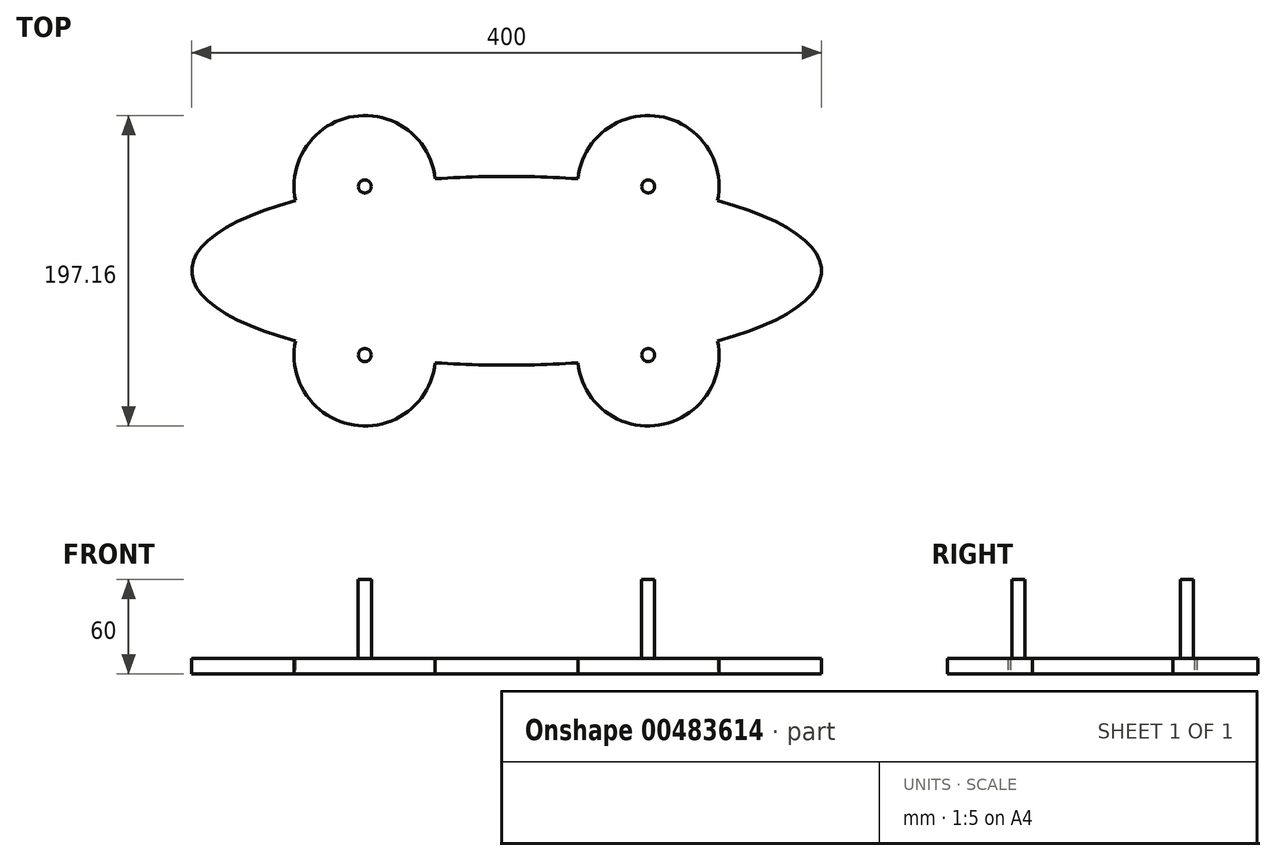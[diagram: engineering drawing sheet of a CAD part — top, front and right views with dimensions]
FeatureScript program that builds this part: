
annotation { "Feature Type Name" : "Feature", "Feature Type Description" : "" }
export const myFeature = defineFeature(function(context is Context, id is Id, definition is map)
    precondition{}
    {
        {
            var Q0;
            Q0=qCreatedBy(makeId("Top.planeOp"),FACE);
            var sketch = newSketch(context, id + "F0", { "sketchPlane" : qUnion([Q0])});
            skLineSegment(sketch, "E0.bottom", {"start": v(200, 100) * mm, "end": v(-200, 100) * mm});
            skLineSegment(sketch, "E0.top", {"start": v(200, -100) * mm, "end": v(-200, -100) * mm});
            skLineSegment(sketch, "E0.left", {"start": v(200, 100) * mm, "end": v(200, -100) * mm});
            skLineSegment(sketch, "E0.right", {"start": v(-200, 100) * mm, "end": v(-200, -100) * mm});
            skPoint(sketch, "E0.middle", {"position": v(0, 0) * mm});
            skLineSegment(sketch, "E1.bottom", {"start": v(200, 60) * mm, "end": v(-200, 60) * mm});
            skLineSegment(sketch, "E1.top", {"start": v(200, -60) * mm, "end": v(-200, -60) * mm});
            skLineSegment(sketch, "E1.left", {"start": v(200, 60) * mm, "end": v(200, -60) * mm});
            skLineSegment(sketch, "E1.right", {"start": v(-200, 60) * mm, "end": v(-200, -60) * mm});
            skPoint(sketch, "E2", {"position": v(200, 0) * mm});
            skPoint(sketch, "E3", {"position": v(0, 60) * mm});
            skEllipse(sketch, "E4", {"center": v(0, 0) * mm, "majorRadius": 200 * mm, "minorRadius": 60 * mm, "majorAxis": v(1, 0)});
            skLineSegment(sketch, "E5.bottom", {"start": v(90, 53.58) * mm, "end": v(-90, 53.58) * mm});
            skLineSegment(sketch, "E5.top", {"start": v(90, -53.58) * mm, "end": v(-90, -53.58) * mm});
            skLineSegment(sketch, "E5.left", {"start": v(90, 53.58) * mm, "end": v(90, -53.58) * mm});
            skLineSegment(sketch, "E5.right", {"start": v(-90, 53.58) * mm, "end": v(-90, -53.58) * mm});
            skCircle(sketch, "E6", {"center": v(-90, 53.58) * mm, "radius": 45 * mm});
            skCircle(sketch, "E7.1.0.0", {"center": v(90, 53.58) * mm, "radius": 45 * mm});
            skLineSegment(sketch, "E7.direction1", {"start": v(-90, 53.58) * mm, "end": v(90, 53.58) * mm, "construction": true});
            skCircle(sketch, "E8.0.1.0", {"center": v(90, -53.58) * mm, "radius": 45 * mm});
            skCircle(sketch, "E8.0.1.1", {"center": v(-90, -53.58) * mm, "radius": 45 * mm});
            skLineSegment(sketch, "E8.direction1", {"start": v(-90, 53.58) * mm, "end": v(-65, 53.58) * mm, "construction": true});
            skLineSegment(sketch, "E8.direction2", {"start": v(-90, 53.58) * mm, "end": v(-90, -53.58) * mm, "construction": true});
            skSolve(sketch);
        }
        {
            var Q0;
            {var subQ5=sQuery(id+"F0.wireOp",EDGE,"E4");var subQ6=makeQuery(id+"F0.imprint","INTERSECT",VERTEX,{"derivedFrom":[sQuery(id+"F0.wireOp",EDGE,"E1.right"),subQ5]});Q0=makeQuery(id+"F0.imprint","IMPRINT",FACE,{"disambiguationData":[TD([[makeQuery(id+"F0.imprint","IMPRINT",EDGE,{"disambiguationData":[TD([[subQ6,1.0]])],"derivedFrom":subQ5}),1.0]])]});}
            var Q1;
            {var subQ1=sQuery(id+"F0.wireOp",EDGE,"E4");var subQ7=makeQuery(id+"F0.imprint","INTERSECT",VERTEX,{"derivedFrom":[sQuery(id+"F0.wireOp",EDGE,"E1.left"),subQ1]});Q1=makeQuery(id+"F0.imprint","IMPRINT",FACE,{"disambiguationData":[TD([[makeQuery(id+"F0.imprint","IMPRINT",EDGE,{"disambiguationData":[TD([[subQ7,-1.0]])],"derivedFrom":subQ1}),1.0]])]});}
            var Q2;
            {var subQ5=sQuery(id+"F0.wireOp",EDGE,"E7.1.0.0");var subQ6=sQuery(id+"F0.wireOp",EDGE,"E5.bottom");var subQ7=makeQuery(id+"F0.imprint","INTERSECT",VERTEX,{"derivedFrom":[subQ6,subQ5]});Q2=makeQuery(id+"F0.imprint","IMPRINT",FACE,{"disambiguationData":[TD([[makeQuery(id+"F0.imprint","IMPRINT",EDGE,{"disambiguationData":[TD([[subQ7,-1.0]])],"derivedFrom":subQ6}),1.0]])]});}
            var Q3;
            {var subQ1=sQuery(id+"F0.wireOp",EDGE,"E5.bottom");var subQ3=sQuery(id+"F0.wireOp",EDGE,"E7.1.0.0");var subQ4=makeQuery(id+"F0.imprint","INTERSECT",VERTEX,{"derivedFrom":[subQ1,subQ3]});Q3=makeQuery(id+"F0.imprint","IMPRINT",FACE,{"disambiguationData":[TD([[makeQuery(id+"F0.imprint","IMPRINT",EDGE,{"disambiguationData":[TD([[subQ4,-1.0]])],"derivedFrom":subQ3}),1.0]])]});}
            var Q4;
            {var subQ1=sQuery(id+"F0.wireOp",EDGE,"E5.top");var subQ3=sQuery(id+"F0.wireOp",EDGE,"E8.0.1.0");var subQ4=makeQuery(id+"F0.imprint","INTERSECT",VERTEX,{"derivedFrom":[subQ1,subQ3]});Q4=makeQuery(id+"F0.imprint","IMPRINT",FACE,{"disambiguationData":[TD([[makeQuery(id+"F0.imprint","IMPRINT",EDGE,{"disambiguationData":[TD([[subQ4,1.0]])],"derivedFrom":subQ3}),1.0]])]});}
            var Q5;
            {var subQ1=sQuery(id+"F0.wireOp",EDGE,"E5.top");var subQ3=sQuery(id+"F0.wireOp",EDGE,"E8.0.1.1");var subQ4=makeQuery(id+"F0.imprint","INTERSECT",VERTEX,{"derivedFrom":[subQ1,subQ3]});Q5=makeQuery(id+"F0.imprint","IMPRINT",FACE,{"disambiguationData":[TD([[makeQuery(id+"F0.imprint","IMPRINT",EDGE,{"disambiguationData":[TD([[subQ4,-1.0]])],"derivedFrom":subQ3}),1.0]])]});}
            var Q6;
            {var subQ1=sQuery(id+"F0.wireOp",EDGE,"E5.bottom");var subQ3=sQuery(id+"F0.wireOp",EDGE,"E6");var subQ4=makeQuery(id+"F0.imprint","INTERSECT",VERTEX,{"derivedFrom":[subQ1,subQ3]});Q6=makeQuery(id+"F0.imprint","IMPRINT",FACE,{"disambiguationData":[TD([[makeQuery(id+"F0.imprint","IMPRINT",EDGE,{"disambiguationData":[TD([[subQ4,1.0]])],"derivedFrom":subQ3}),1.0]])]});}
            var Q7;
            {var subQ1=sQuery(id+"F0.wireOp",EDGE,"E4");var subQ3=sQuery(id+"F0.wireOp",EDGE,"E6");var subQ4=makeQuery(id+"F0.imprint","INTERSECT",VERTEX,{"disambiguationData":[OD(1.0)],"derivedFrom":[subQ1,subQ3]});Q7=makeQuery(id+"F0.imprint","IMPRINT",FACE,{"disambiguationData":[TD([[makeQuery(id+"F0.imprint","IMPRINT",EDGE,{"disambiguationData":[TD([[subQ4,-1.0]])],"derivedFrom":subQ3}),1.0]])]});}
            var Q8;
            {var subQ1=sQuery(id+"F0.wireOp",EDGE,"E4");var subQ3=sQuery(id+"F0.wireOp",EDGE,"E8.0.1.1");var subQ4=makeQuery(id+"F0.imprint","INTERSECT",VERTEX,{"disambiguationData":[OD(0.0)],"derivedFrom":[subQ1,subQ3]});Q8=makeQuery(id+"F0.imprint","IMPRINT",FACE,{"disambiguationData":[TD([[makeQuery(id+"F0.imprint","IMPRINT",EDGE,{"disambiguationData":[TD([[subQ4,1.0]])],"derivedFrom":subQ3}),1.0]])]});}
            var Q9;
            {var subQ1=sQuery(id+"F0.wireOp",EDGE,"E4");var subQ3=sQuery(id+"F0.wireOp",EDGE,"E7.1.0.0");var subQ4=makeQuery(id+"F0.imprint","INTERSECT",VERTEX,{"disambiguationData":[OD(0.0)],"derivedFrom":[subQ1,subQ3]});Q9=makeQuery(id+"F0.imprint","IMPRINT",FACE,{"disambiguationData":[TD([[makeQuery(id+"F0.imprint","IMPRINT",EDGE,{"disambiguationData":[TD([[subQ4,1.0]])],"derivedFrom":subQ3}),1.0]])]});}
            var Q10;
            {var subQ1=sQuery(id+"F0.wireOp",EDGE,"E4");var subQ3=sQuery(id+"F0.wireOp",EDGE,"E8.0.1.0");var subQ4=makeQuery(id+"F0.imprint","INTERSECT",VERTEX,{"disambiguationData":[OD(1.0)],"derivedFrom":[subQ1,subQ3]});Q10=makeQuery(id+"F0.imprint","IMPRINT",FACE,{"disambiguationData":[TD([[makeQuery(id+"F0.imprint","IMPRINT",EDGE,{"disambiguationData":[TD([[subQ4,-1.0]])],"derivedFrom":subQ3}),1.0]])]});}
            var Q11;
            {var subQ1=sQuery(id+"F0.wireOp",EDGE,"E4");var subQ3=sQuery(id+"F0.wireOp",EDGE,"E8.0.1.0");var subQ4=makeQuery(id+"F0.imprint","INTERSECT",VERTEX,{"disambiguationData":[OD(0.0)],"derivedFrom":[subQ1,subQ3]});Q11=makeQuery(id+"F0.imprint","IMPRINT",FACE,{"disambiguationData":[TD([[makeQuery(id+"F0.imprint","IMPRINT",EDGE,{"disambiguationData":[TD([[subQ4,1.0]])],"derivedFrom":subQ3}),1.0]])]});}
            var Q12;
            {var subQ2=sQuery(id+"F0.wireOp",EDGE,"E8.0.1.0");var subQ4=sQuery(id+"F0.wireOp",EDGE,"E1.top");var subQ7=makeQuery(id+"F0.imprint","INTERSECT",VERTEX,{"disambiguationData":[OD(0.0)],"derivedFrom":[subQ4,subQ2]});Q12=makeQuery(id+"F0.imprint","IMPRINT",FACE,{"disambiguationData":[TD([[makeQuery(id+"F0.imprint","IMPRINT",EDGE,{"disambiguationData":[TD([[subQ7,-1.0]])],"derivedFrom":subQ4}),-1.0]])]});}
            var Q13;
            {var subQ1=sQuery(id+"F0.wireOp",EDGE,"E4");var subQ3=sQuery(id+"F0.wireOp",EDGE,"E7.1.0.0");var subQ4=makeQuery(id+"F0.imprint","INTERSECT",VERTEX,{"disambiguationData":[OD(1.0)],"derivedFrom":[subQ1,subQ3]});Q13=makeQuery(id+"F0.imprint","IMPRINT",FACE,{"disambiguationData":[TD([[makeQuery(id+"F0.imprint","IMPRINT",EDGE,{"disambiguationData":[TD([[subQ4,-1.0]])],"derivedFrom":subQ3}),1.0]])]});}
            var Q14;
            {var subQ5=sQuery(id+"F0.wireOp",EDGE,"E4");var subQ7=makeQuery(id+"F0.imprint","INTERSECT",VERTEX,{"derivedFrom":[sQuery(id+"F0.wireOp",EDGE,"E1.bottom"),subQ5]});Q14=makeQuery(id+"F0.imprint","IMPRINT",FACE,{"disambiguationData":[TD([[makeQuery(id+"F0.imprint","IMPRINT",EDGE,{"disambiguationData":[TD([[subQ7,1.0]])],"derivedFrom":subQ5}),1.0]])]});}
            var Q15;
            {var subQ0=sQuery(id+"F0.wireOp",EDGE,"E7.1.0.0");var subQ1=sQuery(id+"F0.wireOp",EDGE,"E1.bottom");var subQ2=makeQuery(id+"F0.imprint","INTERSECT",VERTEX,{"disambiguationData":[OD(0.0)],"derivedFrom":[subQ1,subQ0]});Q15=makeQuery(id+"F0.imprint","IMPRINT",FACE,{"disambiguationData":[TD([[makeQuery(id+"F0.imprint","IMPRINT",EDGE,{"disambiguationData":[TD([[subQ2,-1.0]])],"derivedFrom":subQ1}),-1.0]])]});}
            var Q16;
            {var subQ2=sQuery(id+"F0.wireOp",EDGE,"E7.1.0.0");var subQ4=sQuery(id+"F0.wireOp",EDGE,"E1.bottom");var subQ7=makeQuery(id+"F0.imprint","INTERSECT",VERTEX,{"disambiguationData":[OD(0.0)],"derivedFrom":[subQ4,subQ2]});Q16=makeQuery(id+"F0.imprint","IMPRINT",FACE,{"disambiguationData":[TD([[makeQuery(id+"F0.imprint","IMPRINT",EDGE,{"disambiguationData":[TD([[subQ7,-1.0]])],"derivedFrom":subQ4}),1.0]])]});}
            var Q17;
            {var subQ0=sQuery(id+"F0.wireOp",EDGE,"E6");var subQ1=sQuery(id+"F0.wireOp",EDGE,"E1.bottom");var subQ2=makeQuery(id+"F0.imprint","INTERSECT",VERTEX,{"disambiguationData":[OD(0.0)],"derivedFrom":[subQ1,subQ0]});Q17=makeQuery(id+"F0.imprint","IMPRINT",FACE,{"disambiguationData":[TD([[makeQuery(id+"F0.imprint","IMPRINT",EDGE,{"disambiguationData":[TD([[subQ2,-1.0]])],"derivedFrom":subQ1}),-1.0]])]});}
            var Q18;
            {var subQ0=sQuery(id+"F0.wireOp",EDGE,"E6");var subQ1=sQuery(id+"F0.wireOp",EDGE,"E1.bottom");var subQ2=makeQuery(id+"F0.imprint","INTERSECT",VERTEX,{"disambiguationData":[OD(0.0)],"derivedFrom":[subQ1,subQ0]});Q18=makeQuery(id+"F0.imprint","IMPRINT",FACE,{"disambiguationData":[TD([[makeQuery(id+"F0.imprint","IMPRINT",EDGE,{"disambiguationData":[TD([[subQ2,-1.0]])],"derivedFrom":subQ1}),1.0]])]});}
            var Q19;
            {var subQ1=sQuery(id+"F0.wireOp",EDGE,"E4");var subQ3=sQuery(id+"F0.wireOp",EDGE,"E6");var subQ4=makeQuery(id+"F0.imprint","INTERSECT",VERTEX,{"disambiguationData":[OD(0.0)],"derivedFrom":[subQ1,subQ3]});Q19=makeQuery(id+"F0.imprint","IMPRINT",FACE,{"disambiguationData":[TD([[makeQuery(id+"F0.imprint","IMPRINT",EDGE,{"disambiguationData":[TD([[subQ4,1.0]])],"derivedFrom":subQ3}),1.0]])]});}
            var Q20;
            {var subQ1=sQuery(id+"F0.wireOp",EDGE,"E4");var subQ3=sQuery(id+"F0.wireOp",EDGE,"E8.0.1.1");var subQ4=makeQuery(id+"F0.imprint","INTERSECT",VERTEX,{"disambiguationData":[OD(1.0)],"derivedFrom":[subQ1,subQ3]});Q20=makeQuery(id+"F0.imprint","IMPRINT",FACE,{"disambiguationData":[TD([[makeQuery(id+"F0.imprint","IMPRINT",EDGE,{"disambiguationData":[TD([[subQ4,-1.0]])],"derivedFrom":subQ3}),1.0]])]});}
            var Q21;
            {var subQ0=sQuery(id+"F0.wireOp",EDGE,"E8.0.1.1");var subQ1=sQuery(id+"F0.wireOp",EDGE,"E1.top");var subQ2=makeQuery(id+"F0.imprint","INTERSECT",VERTEX,{"disambiguationData":[OD(0.0)],"derivedFrom":[subQ1,subQ0]});Q21=makeQuery(id+"F0.imprint","IMPRINT",FACE,{"disambiguationData":[TD([[makeQuery(id+"F0.imprint","IMPRINT",EDGE,{"disambiguationData":[TD([[subQ2,-1.0]])],"derivedFrom":subQ1}),1.0]])]});}
            var Q22;
            {var subQ0=sQuery(id+"F0.wireOp",EDGE,"E8.0.1.0");var subQ1=sQuery(id+"F0.wireOp",EDGE,"E1.top");var subQ2=makeQuery(id+"F0.imprint","INTERSECT",VERTEX,{"disambiguationData":[OD(0.0)],"derivedFrom":[subQ1,subQ0]});Q22=makeQuery(id+"F0.imprint","IMPRINT",FACE,{"disambiguationData":[TD([[makeQuery(id+"F0.imprint","IMPRINT",EDGE,{"disambiguationData":[TD([[subQ2,-1.0]])],"derivedFrom":subQ1}),1.0]])]});}
            var Q23;
            {var subQ0=sQuery(id+"F0.wireOp",EDGE,"E8.0.1.1");var subQ1=sQuery(id+"F0.wireOp",EDGE,"E1.top");var subQ7=makeQuery(id+"F0.imprint","INTERSECT",VERTEX,{"disambiguationData":[OD(0.0)],"derivedFrom":[subQ1,subQ0]});Q23=makeQuery(id+"F0.imprint","IMPRINT",FACE,{"disambiguationData":[TD([[makeQuery(id+"F0.imprint","IMPRINT",EDGE,{"disambiguationData":[TD([[subQ7,-1.0]])],"derivedFrom":subQ1}),-1.0]])]});}
            var Q24;
            {var subQ5=sQuery(id+"F0.wireOp",EDGE,"E4");var subQ7=makeQuery(id+"F0.imprint","INTERSECT",VERTEX,{"derivedFrom":[sQuery(id+"F0.wireOp",EDGE,"E1.top"),subQ5]});Q24=makeQuery(id+"F0.imprint","IMPRINT",FACE,{"disambiguationData":[TD([[makeQuery(id+"F0.imprint","IMPRINT",EDGE,{"disambiguationData":[TD([[subQ7,1.0]])],"derivedFrom":subQ5}),1.0]])]});}
            extrude(context, id + "F1", {"entities" : qUnion([Q0, Q1, Q2, Q3, Q4, Q5, Q6, Q7, Q8, Q9, Q10, Q11, Q12, Q13, Q14, Q15, Q16, Q17, Q18, Q19, Q20, Q21, Q22, Q23, Q24]), "depth" : 10 * mm});
        }
        {
            var Q0;
            Q0=makeQuery(id+"F1.opExtrude","CAP_FACE",FACE,{"disambiguationData":[OSD([sQuery(id+"F0.wireOp",EDGE,"E4"),sQuery(id+"F0.wireOp",EDGE,"E6"),sQuery(id+"F0.wireOp",EDGE,"E7.1.0.0"),sQuery(id+"F0.wireOp",EDGE,"E8.0.1.0"),sQuery(id+"F0.wireOp",EDGE,"E8.0.1.1")])],"isStart":false});
            var sketch = newSketch(context, id + "F2", { "sketchPlane" : qUnion([Q0])});
            skPoint(sketch, "E9", {"position": v(-90, 53.58) * mm});
            skPoint(sketch, "E10", {"position": v(90, 53.58) * mm});
            skPoint(sketch, "E11", {"position": v(-90, -53.58) * mm});
            skPoint(sketch, "E12", {"position": v(90, -53.58) * mm});
            skCircle(sketch, "E13", {"center": v(-90, 53.58) * mm, "radius": 4.12 * mm});
            skCircle(sketch, "E14", {"center": v(-90, 53.58) * mm, "radius": 11.12 * mm});
            skCircle(sketch, "E15.0.1.0", {"center": v(-90, -53.58) * mm, "radius": 11.12 * mm});
            skCircle(sketch, "E15.0.1.1", {"center": v(-90, -53.58) * mm, "radius": 4.12 * mm});
            skLineSegment(sketch, "E15.direction1", {"start": v(-90, 53.58) * mm, "end": v(-65, 53.58) * mm, "construction": true});
            skLineSegment(sketch, "E15.direction2", {"start": v(-90, 53.58) * mm, "end": v(-90, -53.58) * mm, "construction": true});
            skCircle(sketch, "E16.1.0.0", {"center": v(90, -53.58) * mm, "radius": 4.12 * mm});
            skCircle(sketch, "E16.1.0.1", {"center": v(90, 53.58) * mm, "radius": 11.12 * mm});
            skCircle(sketch, "E16.1.0.2", {"center": v(90, 53.58) * mm, "radius": 4.12 * mm});
            skCircle(sketch, "E16.1.0.3", {"center": v(90, -53.58) * mm, "radius": 11.12 * mm});
            skLineSegment(sketch, "E16.direction1", {"start": v(-90, -53.58) * mm, "end": v(90, -53.58) * mm, "construction": true});
            skSolve(sketch);
        }
        {
            var Q0;
            Q0=makeQuery(id+"F2.imprint","IMPRINT",FACE,{"disambiguationData":[TD([[makeQuery(id+"F2.imprint","IMPRINT",EDGE,{"derivedFrom":sQuery(id+"F2.wireOp",EDGE,"E16.1.0.2")}),1.0]])]});
            var Q1;
            Q1=makeQuery(id+"F2.imprint","IMPRINT",FACE,{"disambiguationData":[TD([[makeQuery(id+"F2.imprint","IMPRINT",EDGE,{"derivedFrom":sQuery(id+"F2.wireOp",EDGE,"E16.1.0.0")}),1.0]])]});
            var Q2;
            Q2=makeQuery(id+"F2.imprint","IMPRINT",FACE,{"disambiguationData":[TD([[makeQuery(id+"F2.imprint","IMPRINT",EDGE,{"derivedFrom":sQuery(id+"F2.wireOp",EDGE,"E15.0.1.1")}),1.0]])]});
            var Q3;
            Q3=makeQuery(id+"F2.imprint","IMPRINT",FACE,{"disambiguationData":[TD([[makeQuery(id+"F2.imprint","IMPRINT",EDGE,{"derivedFrom":sQuery(id+"F2.wireOp",EDGE,"E13")}),1.0]])]});
            extrude(context, id + "F3", {"entities" : qUnion([Q0, Q1, Q2, Q3]), "operationType" : NewBodyOperationType.ADD, "depth" : 50 * mm});
        }
    });
